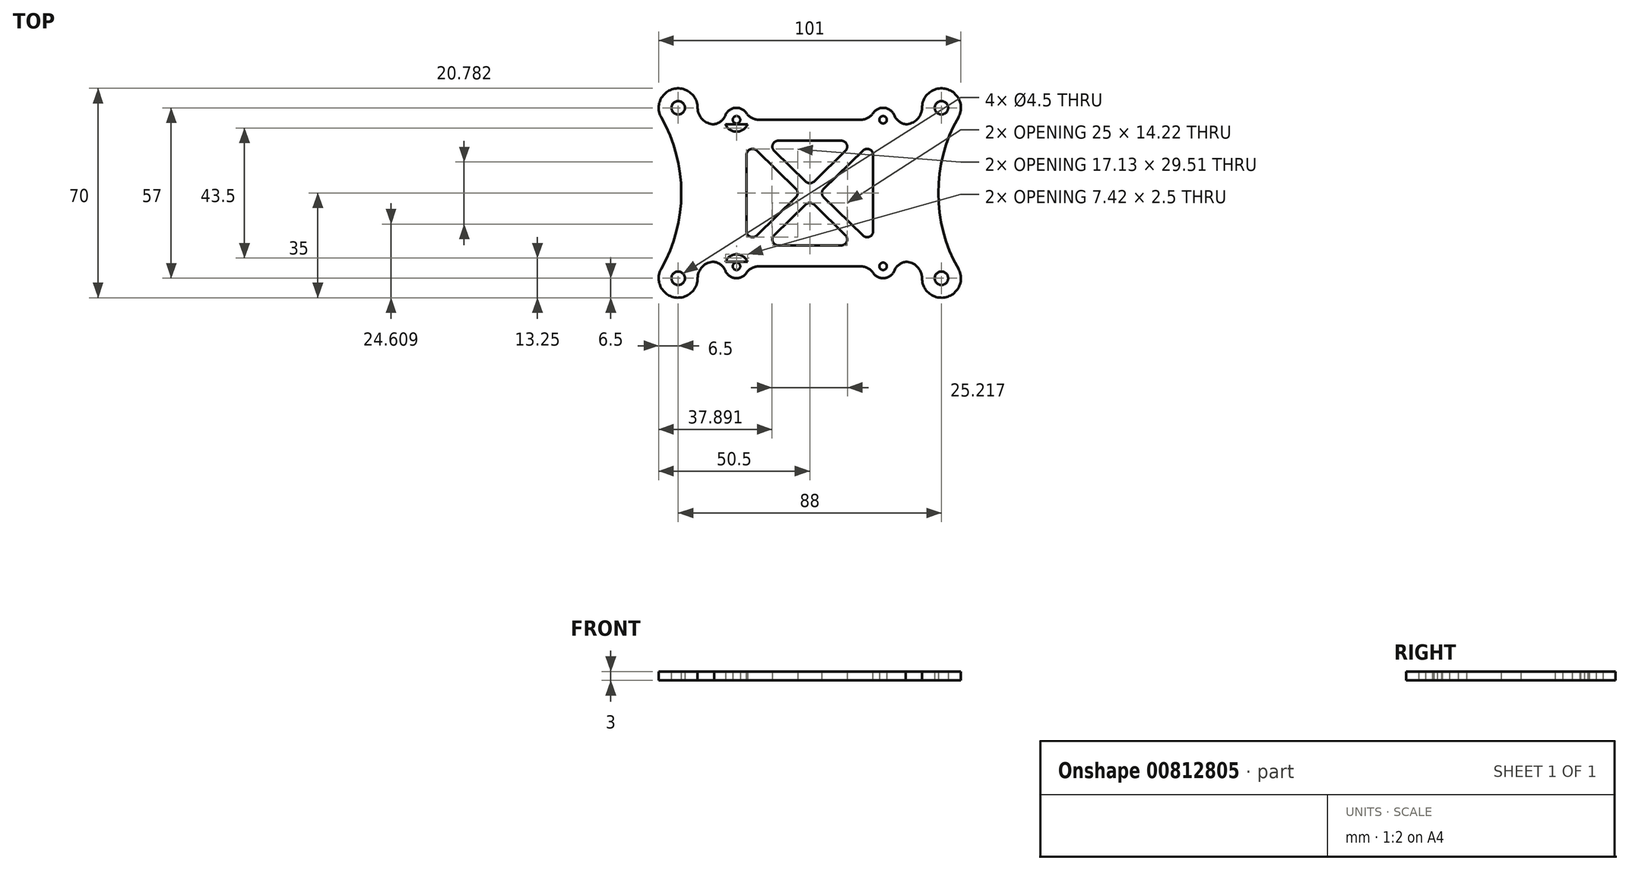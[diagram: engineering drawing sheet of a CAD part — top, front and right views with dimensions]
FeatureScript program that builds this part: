
annotation { "Feature Type Name" : "Feature", "Feature Type Description" : "" }
export const myFeature = defineFeature(function(context is Context, id is Id, definition is map)
    precondition{}
    {
        {
            var Q0;
            Q0=qCreatedBy(makeId("Top.planeOp"),FACE);
            var sketch = newSketch(context, id + "F0", { "sketchPlane" : qUnion([Q0])});
            skCircle(sketch, "E0", {"center": v(0, 0) * mm, "radius": 2.25 * mm});
            skCircle(sketch, "E1", {"center": v(0, 57) * mm, "radius": 2.25 * mm});
            skCircle(sketch, "E2", {"center": v(88, 0) * mm, "radius": 2.25 * mm});
            skCircle(sketch, "E3", {"center": v(88, 57) * mm, "radius": 2.25 * mm});
            skCircle(sketch, "E4", {"center": v(0, 57) * mm, "radius": 6.5 * mm});
            skCircle(sketch, "E5", {"center": v(0, 0) * mm, "radius": 6.5 * mm});
            skCircle(sketch, "E6", {"center": v(88, 57) * mm, "radius": 6.5 * mm});
            skCircle(sketch, "E7", {"center": v(88, 0) * mm, "radius": 6.5 * mm});
            skLineSegment(sketch, "E8", {"start": v(0, 57) * mm, "end": v(0, 38.81) * mm});
            skLineSegment(sketch, "E9", {"start": v(88, 57) * mm, "end": v(88, 38.81) * mm});
            skLineSegment(sketch, "E10", {"start": v(0, 28.5) * mm, "end": v(88, 28.5) * mm});
            skLineSegment(sketch, "E11", {"start": v(3.46, 51.5) * mm, "end": v(84.54, 51.5) * mm});
            skLineSegment(sketch, "E12", {"start": v(3.46, 5.5) * mm, "end": v(84.54, 5.5) * mm});
            skArc(sketch, "E13", {"start": v(-5.65, 3.22) * mm, "mid": v(1.05, 28.5) * mm, "end": v(-5.65, 53.78) * mm});
            skArc(sketch, "E14", {"start": v(93.65, 53.78) * mm, "mid": v(86.95, 28.5) * mm, "end": v(93.65, 3.22) * mm});
            skArc(sketch, "E15", {"start": v(6.5, 57) * mm, "mid": v(8.11, 53.11) * mm, "end": v(12, 51.5) * mm});
            skArc(sketch, "E16", {"start": v(76, 51.5) * mm, "mid": v(79.89, 53.11) * mm, "end": v(81.5, 57) * mm});
            skArc(sketch, "E17", {"start": v(12, 5.5) * mm, "mid": v(8.11, 3.89) * mm, "end": v(6.5, 0) * mm});
            skArc(sketch, "E18", {"start": v(81.5, 0) * mm, "mid": v(79.89, 3.89) * mm, "end": v(76, 5.5) * mm});
            skLineSegment(sketch, "E19.trimOffspring", {"start": v(88, 18.19) * mm, "end": v(88, 0) * mm});
            skLineSegment(sketch, "E20.trimOffspring", {"start": v(0, 18.19) * mm, "end": v(0, 0) * mm});
            skCircle(sketch, "E21", {"center": v(19.5, 53) * mm, "radius": 1.25 * mm});
            skCircle(sketch, "E22", {"center": v(68.5, 53) * mm, "radius": 1.25 * mm});
            skLineSegment(sketch, "E23", {"start": v(19.5, 53) * mm, "end": v(68.5, 53) * mm});
            skLineSegment(sketch, "E24", {"start": v(44, 51.5) * mm, "end": v(44, 53) * mm});
            skCircle(sketch, "E25", {"center": v(19.5, 4) * mm, "radius": 1.25 * mm});
            skCircle(sketch, "E26", {"center": v(68.5, 4) * mm, "radius": 1.25 * mm});
            skLineSegment(sketch, "E27", {"start": v(19.5, 4) * mm, "end": v(68.5, 4) * mm});
            skLineSegment(sketch, "E28", {"start": v(44, 4) * mm, "end": v(44, 5.5) * mm});
            skCircle(sketch, "E29", {"center": v(19.5, 53) * mm, "radius": 4 * mm});
            skCircle(sketch, "E30", {"center": v(68.5, 53) * mm, "radius": 4 * mm});
            skCircle(sketch, "E31", {"center": v(19.5, 4) * mm, "radius": 4 * mm});
            skCircle(sketch, "E32", {"center": v(68.5, 4) * mm, "radius": 4 * mm});
            skLineSegment(sketch, "E33", {"start": v(15.5, 4) * mm, "end": v(15.5, 5.5) * mm});
            skLineSegment(sketch, "E34", {"start": v(15.5, 53) * mm, "end": v(15.5, 51.5) * mm});
            skLineSegment(sketch, "E35", {"start": v(72.5, 53) * mm, "end": v(72.5, 51.5) * mm});
            skLineSegment(sketch, "E36", {"start": v(72.5, 4) * mm, "end": v(72.5, 5.5) * mm});
            skSolve(sketch);
        }
        {
            var Q0;
            {var subQ0=sQuery(id+"F0.wireOp",EDGE,"E11");var subQ14=sQuery(id+"F0.wireOp",EDGE,"E4");var subQ15=makeQuery(id+"F0.imprint","INTERSECT",VERTEX,{"derivedFrom":[subQ14,subQ0]});Q0=makeQuery(id+"F0.imprint","IMPRINT",FACE,{"disambiguationData":[TD([[makeQuery(id+"F0.imprint","IMPRINT",EDGE,{"disambiguationData":[TD([[subQ15,1.0]])],"derivedFrom":subQ14}),-1.0]])]});}
            var Q1;
            {var subQ0=sQuery(id+"F0.wireOp",EDGE,"E13");var subQ1=sQuery(id+"F0.wireOp",EDGE,"E4");var subQ2=makeQuery(id+"F0.imprint","INTERSECT",VERTEX,{"derivedFrom":[subQ1,subQ0]});Q1=makeQuery(id+"F0.imprint","IMPRINT",FACE,{"disambiguationData":[TD([[makeQuery(id+"F0.imprint","IMPRINT",EDGE,{"disambiguationData":[TD([[subQ2,-1.0]])],"derivedFrom":subQ1}),-1.0]])]});}
            var Q2;
            {var subQ3=sQuery(id+"F0.wireOp",EDGE,"E15");Q2=makeQuery(id+"F0.imprint","IMPRINT",FACE,{"disambiguationData":[TD([[makeQuery(id+"F0.imprint","IMPRINT",EDGE,{"derivedFrom":subQ3}),-1.0]])]});}
            var Q3;
            Q3=makeQuery(id+"F0.imprint","IMPRINT",FACE,{"disambiguationData":[TD([[makeQuery(id+"F0.imprint","IMPRINT",EDGE,{"derivedFrom":sQuery(id+"F0.wireOp",EDGE,"E1")}),-1.0]])]});
            var Q4;
            {var subQ0=sQuery(id+"F0.wireOp",EDGE,"E29");var subQ1=sQuery(id+"F0.wireOp",EDGE,"E11");var subQ2=makeQuery(id+"F0.imprint","INTERSECT",VERTEX,{"disambiguationData":[OD(0.0)],"derivedFrom":[subQ1,subQ0]});Q4=makeQuery(id+"F0.imprint","IMPRINT",FACE,{"disambiguationData":[TD([[makeQuery(id+"F0.imprint","IMPRINT",EDGE,{"disambiguationData":[TD([[subQ2,-1.0]])],"derivedFrom":subQ1}),-1.0]])]});}
            var Q5;
            Q5=makeQuery(id+"F0.imprint","IMPRINT",FACE,{"disambiguationData":[TD([[makeQuery(id+"F0.imprint","IMPRINT",EDGE,{"derivedFrom":sQuery(id+"F0.wireOp",EDGE,"E21")}),-1.0]])]});
            var Q6;
            {var subQ0=sQuery(id+"F0.wireOp",EDGE,"E24");Q6=makeQuery(id+"F0.imprint","IMPRINT",FACE,{"disambiguationData":[TD([[makeQuery(id+"F0.imprint","IMPRINT",EDGE,{"derivedFrom":subQ0}),1.0]])]});}
            var Q7;
            {var subQ0=sQuery(id+"F0.wireOp",EDGE,"E24");Q7=makeQuery(id+"F0.imprint","IMPRINT",FACE,{"disambiguationData":[TD([[makeQuery(id+"F0.imprint","IMPRINT",EDGE,{"derivedFrom":subQ0}),-1.0]])]});}
            var Q8;
            {var subQ0=sQuery(id+"F0.wireOp",EDGE,"E30");var subQ1=sQuery(id+"F0.wireOp",EDGE,"E11");var subQ2=makeQuery(id+"F0.imprint","INTERSECT",VERTEX,{"disambiguationData":[OD(0.0)],"derivedFrom":[subQ1,subQ0]});Q8=makeQuery(id+"F0.imprint","IMPRINT",FACE,{"disambiguationData":[TD([[makeQuery(id+"F0.imprint","IMPRINT",EDGE,{"disambiguationData":[TD([[subQ2,-1.0]])],"derivedFrom":subQ1}),-1.0]])]});}
            var Q9;
            Q9=makeQuery(id+"F0.imprint","IMPRINT",FACE,{"disambiguationData":[TD([[makeQuery(id+"F0.imprint","IMPRINT",EDGE,{"derivedFrom":sQuery(id+"F0.wireOp",EDGE,"E22")}),-1.0]])]});
            var Q10;
            {var subQ3=sQuery(id+"F0.wireOp",EDGE,"E16");Q10=makeQuery(id+"F0.imprint","IMPRINT",FACE,{"disambiguationData":[TD([[makeQuery(id+"F0.imprint","IMPRINT",EDGE,{"derivedFrom":subQ3}),-1.0]])]});}
            var Q11;
            Q11=makeQuery(id+"F0.imprint","IMPRINT",FACE,{"disambiguationData":[TD([[makeQuery(id+"F0.imprint","IMPRINT",EDGE,{"derivedFrom":sQuery(id+"F0.wireOp",EDGE,"E3")}),-1.0]])]});
            var Q12;
            {var subQ0=sQuery(id+"F0.wireOp",EDGE,"E14");var subQ1=sQuery(id+"F0.wireOp",EDGE,"E6");var subQ2=makeQuery(id+"F0.imprint","INTERSECT",VERTEX,{"derivedFrom":[subQ1,subQ0]});Q12=makeQuery(id+"F0.imprint","IMPRINT",FACE,{"disambiguationData":[TD([[makeQuery(id+"F0.imprint","IMPRINT",EDGE,{"disambiguationData":[TD([[subQ2,1.0]])],"derivedFrom":subQ1}),-1.0]])]});}
            var Q13;
            {var subQ0=sQuery(id+"F0.wireOp",EDGE,"E14");var subQ1=sQuery(id+"F0.wireOp",EDGE,"E7");var subQ2=makeQuery(id+"F0.imprint","INTERSECT",VERTEX,{"derivedFrom":[subQ1,subQ0]});Q13=makeQuery(id+"F0.imprint","IMPRINT",FACE,{"disambiguationData":[TD([[makeQuery(id+"F0.imprint","IMPRINT",EDGE,{"disambiguationData":[TD([[subQ2,-1.0]])],"derivedFrom":subQ1}),-1.0]])]});}
            var Q14;
            {var subQ0=sQuery(id+"F0.wireOp",EDGE,"E12");var subQ16=sQuery(id+"F0.wireOp",EDGE,"E5");var subQ17=makeQuery(id+"F0.imprint","INTERSECT",VERTEX,{"derivedFrom":[subQ16,subQ0]});Q14=makeQuery(id+"F0.imprint","IMPRINT",FACE,{"disambiguationData":[TD([[makeQuery(id+"F0.imprint","IMPRINT",EDGE,{"disambiguationData":[TD([[subQ17,-1.0]])],"derivedFrom":subQ16}),-1.0]])]});}
            var Q15;
            {var subQ0=sQuery(id+"F0.wireOp",EDGE,"E13");var subQ1=sQuery(id+"F0.wireOp",EDGE,"E5");var subQ2=makeQuery(id+"F0.imprint","INTERSECT",VERTEX,{"derivedFrom":[subQ1,subQ0]});Q15=makeQuery(id+"F0.imprint","IMPRINT",FACE,{"disambiguationData":[TD([[makeQuery(id+"F0.imprint","IMPRINT",EDGE,{"disambiguationData":[TD([[subQ2,1.0]])],"derivedFrom":subQ1}),-1.0]])]});}
            var Q16;
            {var subQ3=sQuery(id+"F0.wireOp",EDGE,"E17");Q16=makeQuery(id+"F0.imprint","IMPRINT",FACE,{"disambiguationData":[TD([[makeQuery(id+"F0.imprint","IMPRINT",EDGE,{"derivedFrom":subQ3}),-1.0]])]});}
            var Q17;
            {var subQ3=sQuery(id+"F0.wireOp",EDGE,"E18");Q17=makeQuery(id+"F0.imprint","IMPRINT",FACE,{"disambiguationData":[TD([[makeQuery(id+"F0.imprint","IMPRINT",EDGE,{"derivedFrom":subQ3}),-1.0]])]});}
            var Q18;
            Q18=makeQuery(id+"F0.imprint","IMPRINT",FACE,{"disambiguationData":[TD([[makeQuery(id+"F0.imprint","IMPRINT",EDGE,{"derivedFrom":sQuery(id+"F0.wireOp",EDGE,"E26")}),-1.0]])]});
            var Q19;
            {var subQ0=sQuery(id+"F0.wireOp",EDGE,"E28");Q19=makeQuery(id+"F0.imprint","IMPRINT",FACE,{"disambiguationData":[TD([[makeQuery(id+"F0.imprint","IMPRINT",EDGE,{"derivedFrom":subQ0}),-1.0]])]});}
            var Q20;
            {var subQ0=sQuery(id+"F0.wireOp",EDGE,"E32");var subQ1=sQuery(id+"F0.wireOp",EDGE,"E12");var subQ2=makeQuery(id+"F0.imprint","INTERSECT",VERTEX,{"disambiguationData":[OD(0.0)],"derivedFrom":[subQ1,subQ0]});Q20=makeQuery(id+"F0.imprint","IMPRINT",FACE,{"disambiguationData":[TD([[makeQuery(id+"F0.imprint","IMPRINT",EDGE,{"disambiguationData":[TD([[subQ2,-1.0]])],"derivedFrom":subQ1}),1.0]])]});}
            var Q21;
            {var subQ0=sQuery(id+"F0.wireOp",EDGE,"E28");Q21=makeQuery(id+"F0.imprint","IMPRINT",FACE,{"disambiguationData":[TD([[makeQuery(id+"F0.imprint","IMPRINT",EDGE,{"derivedFrom":subQ0}),1.0]])]});}
            var Q22;
            Q22=makeQuery(id+"F0.imprint","IMPRINT",FACE,{"disambiguationData":[TD([[makeQuery(id+"F0.imprint","IMPRINT",EDGE,{"derivedFrom":sQuery(id+"F0.wireOp",EDGE,"E25")}),-1.0]])]});
            var Q23;
            {var subQ0=sQuery(id+"F0.wireOp",EDGE,"E31");var subQ1=sQuery(id+"F0.wireOp",EDGE,"E12");var subQ2=makeQuery(id+"F0.imprint","INTERSECT",VERTEX,{"disambiguationData":[OD(0.0)],"derivedFrom":[subQ1,subQ0]});Q23=makeQuery(id+"F0.imprint","IMPRINT",FACE,{"disambiguationData":[TD([[makeQuery(id+"F0.imprint","IMPRINT",EDGE,{"disambiguationData":[TD([[subQ2,-1.0]])],"derivedFrom":subQ1}),1.0]])]});}
            var Q24;
            Q24=makeQuery(id+"F0.imprint","IMPRINT",FACE,{"disambiguationData":[TD([[makeQuery(id+"F0.imprint","IMPRINT",EDGE,{"derivedFrom":sQuery(id+"F0.wireOp",EDGE,"E0")}),-1.0]])]});
            var Q25;
            Q25=makeQuery(id+"F0.imprint","IMPRINT",FACE,{"disambiguationData":[TD([[makeQuery(id+"F0.imprint","IMPRINT",EDGE,{"derivedFrom":sQuery(id+"F0.wireOp",EDGE,"E2")}),-1.0]])]});
            var Q26;
            {var subQ0=sQuery(id+"F0.wireOp",EDGE,"E35");Q26=makeQuery(id+"F0.imprint","IMPRINT",FACE,{"disambiguationData":[TD([[makeQuery(id+"F0.imprint","IMPRINT",EDGE,{"derivedFrom":subQ0}),-1.0]])]});}
            var Q27;
            {var subQ0=sQuery(id+"F0.wireOp",EDGE,"E36");Q27=makeQuery(id+"F0.imprint","IMPRINT",FACE,{"disambiguationData":[TD([[makeQuery(id+"F0.imprint","IMPRINT",EDGE,{"derivedFrom":subQ0}),1.0]])]});}
            var Q28;
            {var subQ0=sQuery(id+"F0.wireOp",EDGE,"E33");Q28=makeQuery(id+"F0.imprint","IMPRINT",FACE,{"disambiguationData":[TD([[makeQuery(id+"F0.imprint","IMPRINT",EDGE,{"derivedFrom":subQ0}),-1.0]])]});}
            var Q29;
            {var subQ0=sQuery(id+"F0.wireOp",EDGE,"E34");Q29=makeQuery(id+"F0.imprint","IMPRINT",FACE,{"disambiguationData":[TD([[makeQuery(id+"F0.imprint","IMPRINT",EDGE,{"derivedFrom":subQ0}),1.0]])]});}
            extrude(context, id + "F1", {"entities" : qUnion([Q0, Q1, Q2, Q3, Q4, Q5, Q6, Q7, Q8, Q9, Q10, Q11, Q12, Q13, Q14, Q15, Q16, Q17, Q18, Q19, Q20, Q21, Q22, Q23, Q24, Q25, Q26, Q27, Q28, Q29]), "depth" : 3 * mm, "offsetDistance" : 25 * mm});
        }
        {
            var Q0;
            Q0=makeQuery(id+"F1.opExtrude","SWEPT_EDGE",EDGE,{"disambiguationData":[OSD([sQuery(id+"F0.wireOp",EDGE,"E11"),sQuery(id+"F0.wireOp",EDGE,"E34")])]});
            var Q1;
            Q1=makeQuery(id+"F1.opExtrude","SWEPT_EDGE",EDGE,{"disambiguationData":[OSD([sQuery(id+"F0.wireOp",EDGE,"E12"),sQuery(id+"F0.wireOp",EDGE,"E33")])]});
            var Q2;
            Q2=makeQuery(id+"F1.opExtrude","SWEPT_EDGE",EDGE,{"disambiguationData":[OSD([sQuery(id+"F0.wireOp",EDGE,"E12"),sQuery(id+"F0.wireOp",EDGE,"E36")])]});
            var Q3;
            Q3=makeQuery(id+"F1.opExtrude","SWEPT_EDGE",EDGE,{"disambiguationData":[OSD([sQuery(id+"F0.wireOp",EDGE,"E27"),sQuery(id+"F0.wireOp",EDGE,"E31")])]});
            var Q4;
            Q4=makeQuery(id+"F1.opExtrude","SWEPT_EDGE",EDGE,{"disambiguationData":[OSD([sQuery(id+"F0.wireOp",EDGE,"E27"),sQuery(id+"F0.wireOp",EDGE,"E32")])]});
            var Q5;
            Q5=makeQuery(id+"F1.opExtrude","SWEPT_EDGE",EDGE,{"disambiguationData":[OSD([sQuery(id+"F0.wireOp",EDGE,"E23"),sQuery(id+"F0.wireOp",EDGE,"E29")])]});
            var Q6;
            Q6=makeQuery(id+"F1.opExtrude","SWEPT_EDGE",EDGE,{"disambiguationData":[OSD([sQuery(id+"F0.wireOp",EDGE,"E11"),sQuery(id+"F0.wireOp",EDGE,"E35")])]});
            var Q7;
            Q7=makeQuery(id+"F1.opExtrude","SWEPT_EDGE",EDGE,{"disambiguationData":[OSD([sQuery(id+"F0.wireOp",EDGE,"E23"),sQuery(id+"F0.wireOp",EDGE,"E30")])]});
            fillet(context, id + "F2", {"entities" : qUnion([Q0, Q1, Q2, Q3, Q4, Q5, Q6, Q7]), "radius" : 5 * mm, "tangentPropagation" : true, "allowEdgeOverflow" : false});
        }
        {
            var Q0;
            Q0=makeQuery(id+"F1.opExtrude","CAP_FACE",FACE,{"disambiguationData":[OSD([sQuery(id+"F0.wireOp",EDGE,"E0"),sQuery(id+"F0.wireOp",EDGE,"E1"),sQuery(id+"F0.wireOp",EDGE,"E2"),sQuery(id+"F0.wireOp",EDGE,"E3"),sQuery(id+"F0.wireOp",EDGE,"E4"),sQuery(id+"F0.wireOp",EDGE,"E5"),sQuery(id+"F0.wireOp",EDGE,"E6"),sQuery(id+"F0.wireOp",EDGE,"E7"),sQuery(id+"F0.wireOp",EDGE,"E11"),sQuery(id+"F0.wireOp",EDGE,"E12"),sQuery(id+"F0.wireOp",EDGE,"E13"),sQuery(id+"F0.wireOp",EDGE,"E14"),sQuery(id+"F0.wireOp",EDGE,"E15"),sQuery(id+"F0.wireOp",EDGE,"E16"),sQuery(id+"F0.wireOp",EDGE,"E17"),sQuery(id+"F0.wireOp",EDGE,"E18"),sQuery(id+"F0.wireOp",EDGE,"E21"),sQuery(id+"F0.wireOp",EDGE,"E22"),sQuery(id+"F0.wireOp",EDGE,"E23"),sQuery(id+"F0.wireOp",EDGE,"E25"),sQuery(id+"F0.wireOp",EDGE,"E26"),sQuery(id+"F0.wireOp",EDGE,"E27"),sQuery(id+"F0.wireOp",EDGE,"E29"),sQuery(id+"F0.wireOp",EDGE,"E30"),sQuery(id+"F0.wireOp",EDGE,"E31"),sQuery(id+"F0.wireOp",EDGE,"E32"),sQuery(id+"F0.wireOp",EDGE,"E33"),sQuery(id+"F0.wireOp",EDGE,"E34"),sQuery(id+"F0.wireOp",EDGE,"E35"),sQuery(id+"F0.wireOp",EDGE,"E36")])],"isStart":false});
            var sketch = newSketch(context, id + "F3", { "sketchPlane" : qUnion([Q0])});
            skLineSegment(sketch, "E37", {"start": v(22.83, 46) * mm, "end": v(22.83, 11) * mm});
            skLineSegment(sketch, "E38", {"start": v(22.83, 11) * mm, "end": v(40.83, 28.5) * mm});
            skPoint(sketch, "E38.endSnap0", {"position": v(22.83, 28.5) * mm});
            skLineSegment(sketch, "E39", {"start": v(40.83, 28.5) * mm, "end": v(22.83, 46) * mm});
            skLineSegment(sketch, "E40", {"start": v(65.17, 46) * mm, "end": v(65.17, 11) * mm});
            skLineSegment(sketch, "E41", {"start": v(65.17, 11) * mm, "end": v(47.17, 28.5) * mm});
            skLineSegment(sketch, "E42", {"start": v(47.17, 28.5) * mm, "end": v(65.17, 46) * mm});
            skCircle(sketch, "E43.0", {"center": v(19.5, 53) * mm, "radius": 1.25 * mm});
            skCircle(sketch, "E44.0", {"center": v(19.5, 4) * mm, "radius": 1.25 * mm});
            skLineSegment(sketch, "E45", {"start": v(19.5, 53) * mm, "end": v(19.5, 4) * mm});
            skLineSegment(sketch, "E46", {"start": v(19.5, 28.5) * mm, "end": v(22.83, 28.5) * mm});
            skLineSegment(sketch, "E47", {"start": v(28.56, 46) * mm, "end": v(59.44, 46) * mm});
            skLineSegment(sketch, "E48", {"start": v(59.44, 46) * mm, "end": v(44, 31) * mm});
            skPoint(sketch, "E48.endSnap0", {"position": v(44, 46) * mm});
            skLineSegment(sketch, "E49", {"start": v(44, 31) * mm, "end": v(28.56, 46) * mm});
            skLineSegment(sketch, "E50", {"start": v(28.56, 11) * mm, "end": v(59.44, 11) * mm});
            skLineSegment(sketch, "E51", {"start": v(59.44, 11) * mm, "end": v(44, 26) * mm});
            skLineSegment(sketch, "E52", {"start": v(44, 26) * mm, "end": v(28.56, 11) * mm});
            skSolve(sketch);
        }
        {
            var Q0;
            Q0=makeQuery(id+"F3.imprint","IMPRINT",FACE,{"disambiguationData":[TD([[makeQuery(id+"F3.imprint","IMPRINT",EDGE,{"derivedFrom":sQuery(id+"F3.wireOp",EDGE,"E47")}),-1.0]])]});
            var Q1;
            {var subQ3=sQuery(id+"F3.wireOp",EDGE,"E38");Q1=makeQuery(id+"F3.imprint","IMPRINT",FACE,{"disambiguationData":[TD([[makeQuery(id+"F3.imprint","IMPRINT",EDGE,{"derivedFrom":subQ3}),1.0]])]});}
            var Q2;
            Q2=makeQuery(id+"F3.imprint","IMPRINT",FACE,{"disambiguationData":[TD([[makeQuery(id+"F3.imprint","IMPRINT",EDGE,{"derivedFrom":sQuery(id+"F3.wireOp",EDGE,"E50")}),1.0]])]});
            var Q3;
            Q3=makeQuery(id+"F3.imprint","IMPRINT",FACE,{"disambiguationData":[TD([[makeQuery(id+"F3.imprint","IMPRINT",EDGE,{"derivedFrom":sQuery(id+"F3.wireOp",EDGE,"E40")}),-1.0]])]});
            extrude(context, id + "F4", {"entities" : qUnion([Q0, Q1, Q2, Q3]), "operationType" : NewBodyOperationType.REMOVE, "oppositeDirection" : true, "depth" : 25 * mm, "offsetDistance" : 25 * mm});
        }
        {
            var Q0;
            Q0=makeQuery(id+"F4.boolean.opBoolean","COPY",EDGE,{"derivedFrom":makeQuery(id+"F4.opExtrude","SWEPT_EDGE",EDGE,{"disambiguationData":[OSD([sQuery(id+"F3.wireOp",EDGE,"E37"),sQuery(id+"F3.wireOp",EDGE,"E39")])]})});
            var Q1;
            Q1=makeQuery(id+"F4.boolean.opBoolean","COPY",EDGE,{"derivedFrom":makeQuery(id+"F4.opExtrude","SWEPT_EDGE",EDGE,{"disambiguationData":[OSD([sQuery(id+"F3.wireOp",EDGE,"E37"),sQuery(id+"F3.wireOp",EDGE,"E38")])]})});
            var Q2;
            Q2=makeQuery(id+"F4.boolean.opBoolean","COPY",EDGE,{"derivedFrom":makeQuery(id+"F4.opExtrude","SWEPT_EDGE",EDGE,{"disambiguationData":[OSD([sQuery(id+"F3.wireOp",EDGE,"E47"),sQuery(id+"F3.wireOp",EDGE,"E49")])]})});
            var Q3;
            Q3=makeQuery(id+"F4.boolean.opBoolean","COPY",EDGE,{"derivedFrom":makeQuery(id+"F4.opExtrude","SWEPT_EDGE",EDGE,{"disambiguationData":[OSD([sQuery(id+"F3.wireOp",EDGE,"E38"),sQuery(id+"F3.wireOp",EDGE,"E39")])]})});
            var Q4;
            Q4=makeQuery(id+"F4.boolean.opBoolean","COPY",EDGE,{"derivedFrom":makeQuery(id+"F4.opExtrude","SWEPT_EDGE",EDGE,{"disambiguationData":[OSD([sQuery(id+"F3.wireOp",EDGE,"E47"),sQuery(id+"F3.wireOp",EDGE,"E48")])]})});
            var Q5;
            Q5=makeQuery(id+"F4.boolean.opBoolean","COPY",EDGE,{"derivedFrom":makeQuery(id+"F4.opExtrude","SWEPT_EDGE",EDGE,{"disambiguationData":[OSD([sQuery(id+"F3.wireOp",EDGE,"E48"),sQuery(id+"F3.wireOp",EDGE,"E49")])]})});
            var Q6;
            Q6=makeQuery(id+"F4.boolean.opBoolean","COPY",EDGE,{"derivedFrom":makeQuery(id+"F4.opExtrude","SWEPT_EDGE",EDGE,{"disambiguationData":[OSD([sQuery(id+"F3.wireOp",EDGE,"E50"),sQuery(id+"F3.wireOp",EDGE,"E52")])]})});
            var Q7;
            Q7=makeQuery(id+"F4.boolean.opBoolean","COPY",EDGE,{"derivedFrom":makeQuery(id+"F4.opExtrude","SWEPT_EDGE",EDGE,{"disambiguationData":[OSD([sQuery(id+"F3.wireOp",EDGE,"E51"),sQuery(id+"F3.wireOp",EDGE,"E52")])]})});
            var Q8;
            Q8=makeQuery(id+"F4.boolean.opBoolean","COPY",EDGE,{"derivedFrom":makeQuery(id+"F4.opExtrude","SWEPT_EDGE",EDGE,{"disambiguationData":[OSD([sQuery(id+"F3.wireOp",EDGE,"E50"),sQuery(id+"F3.wireOp",EDGE,"E51")])]})});
            var Q9;
            Q9=makeQuery(id+"F4.boolean.opBoolean","COPY",EDGE,{"derivedFrom":makeQuery(id+"F4.opExtrude","SWEPT_EDGE",EDGE,{"disambiguationData":[OSD([sQuery(id+"F3.wireOp",EDGE,"E41"),sQuery(id+"F3.wireOp",EDGE,"E42")])]})});
            var Q10;
            Q10=makeQuery(id+"F4.boolean.opBoolean","COPY",EDGE,{"derivedFrom":makeQuery(id+"F4.opExtrude","SWEPT_EDGE",EDGE,{"disambiguationData":[OSD([sQuery(id+"F3.wireOp",EDGE,"E40"),sQuery(id+"F3.wireOp",EDGE,"E42")])]})});
            var Q11;
            Q11=makeQuery(id+"F4.boolean.opBoolean","COPY",EDGE,{"derivedFrom":makeQuery(id+"F4.opExtrude","SWEPT_EDGE",EDGE,{"disambiguationData":[OSD([sQuery(id+"F3.wireOp",EDGE,"E40"),sQuery(id+"F3.wireOp",EDGE,"E41")])]})});
            fillet(context, id + "F5", {"entities" : qUnion([Q0, Q1, Q2, Q3, Q4, Q5, Q6, Q7, Q8, Q9, Q10, Q11]), "radius" : 2 * mm, "tangentPropagation" : true, "allowEdgeOverflow" : false});
        }
    });
